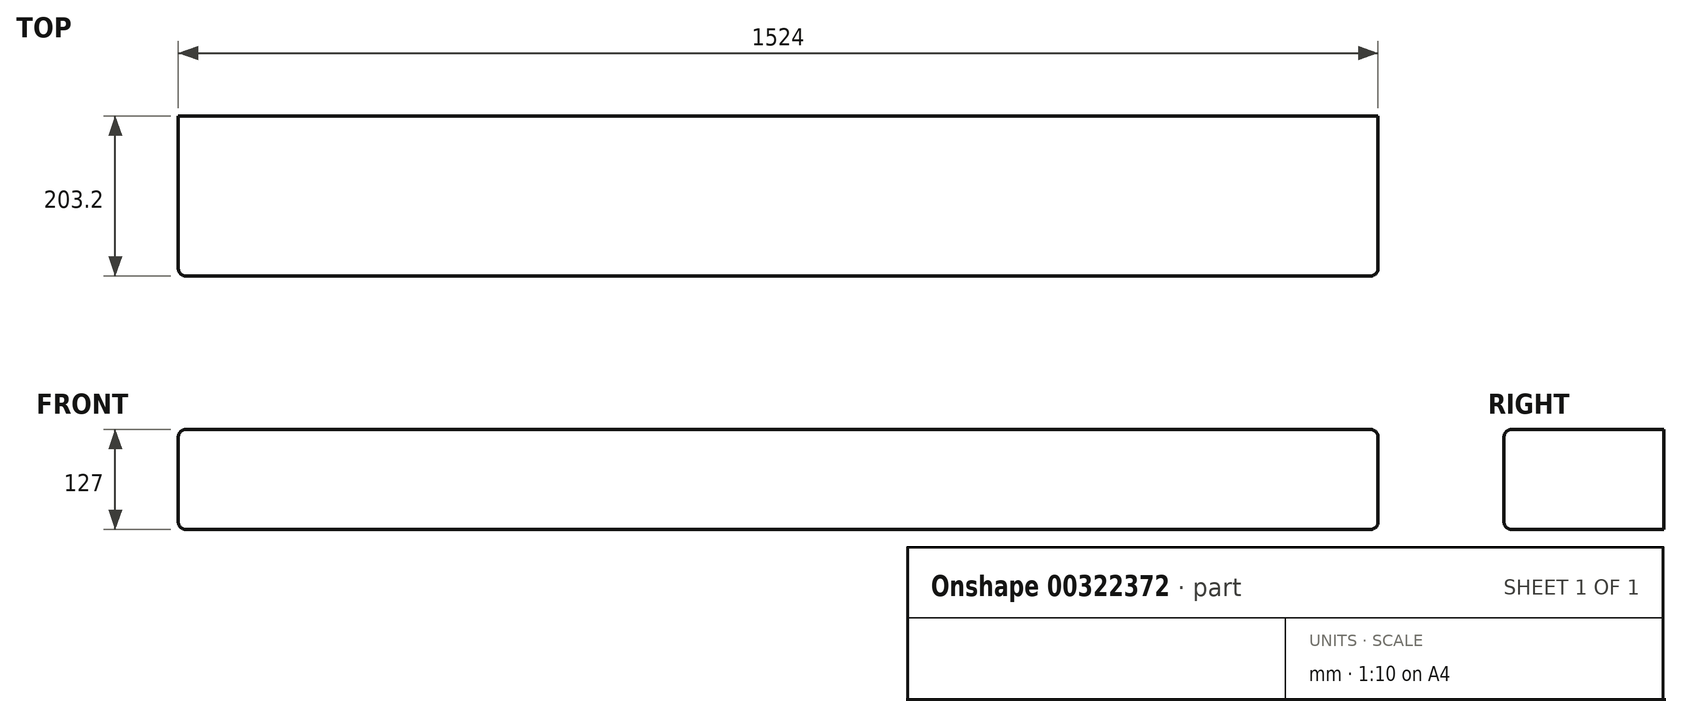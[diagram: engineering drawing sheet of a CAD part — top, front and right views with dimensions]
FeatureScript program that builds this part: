
annotation { "Feature Type Name" : "Feature", "Feature Type Description" : "" }
export const myFeature = defineFeature(function(context is Context, id is Id, definition is map)
    precondition{}
    {
        {
            var Q0;
            Q0=qCreatedBy(makeId("Right.planeOp"),FACE);
            var sketch = newSketch(context, id + "F0", { "sketchPlane" : qUnion([Q0])});
            skLineSegment(sketch, "E0.bottom", {"start": v(0, 0) * mm, "end": v(-203.2, 0) * mm});
            skLineSegment(sketch, "E0.top", {"start": v(0, 127) * mm, "end": v(-203.2, 127) * mm});
            skLineSegment(sketch, "E0.left", {"start": v(0, 0) * mm, "end": v(0, 127) * mm});
            skLineSegment(sketch, "E0.right", {"start": v(-203.2, 0) * mm, "end": v(-203.2, 127) * mm});
            skSolve(sketch);
        }
        {
            var Q0;
            Q0=makeQuery(id+"F0.imprint","IMPRINT",FACE,{"disambiguationData":[TD([[makeQuery(id+"F0.imprint","IMPRINT",EDGE,{"derivedFrom":sQuery(id+"F0.wireOp",EDGE,"E0.bottom")}),-1.0]])]});
            extrude(context, id + "F1", {"entities" : qUnion([Q0]), "endBound" : BoundingType.SYMMETRIC, "depth" : 1524 * mm});
        }
        {
            var Q0;
            Q0=makeQuery(id+"F1.opExtrude","SWEPT_EDGE",EDGE,{"disambiguationData":[OSD([sQuery(id+"F0.wireOp",EDGE,"E0.top"),sQuery(id+"F0.wireOp",EDGE,"E0.right")])]});
            var Q1;
            Q1=makeQuery(id+"F1.opExtrude","CAP_EDGE",EDGE,{"disambiguationData":[OSD([sQuery(id+"F0.wireOp",EDGE,"E0.top")])],"isStart":false});
            var Q2;
            Q2=makeQuery(id+"F1.opExtrude","CAP_EDGE",EDGE,{"disambiguationData":[OSD([sQuery(id+"F0.wireOp",EDGE,"E0.right")])],"isStart":false});
            var Q3;
            Q3=makeQuery(id+"F1.opExtrude","CAP_EDGE",EDGE,{"disambiguationData":[OSD([sQuery(id+"F0.wireOp",EDGE,"E0.bottom")])],"isStart":false});
            var Q4;
            Q4=makeQuery(id+"F1.opExtrude","SWEPT_EDGE",EDGE,{"disambiguationData":[OSD([sQuery(id+"F0.wireOp",EDGE,"E0.bottom"),sQuery(id+"F0.wireOp",EDGE,"E0.right")])]});
            var Q5;
            Q5=makeQuery(id+"F1.opExtrude","CAP_EDGE",EDGE,{"disambiguationData":[OSD([sQuery(id+"F0.wireOp",EDGE,"E0.right")])],"isStart":true});
            var Q6;
            Q6=makeQuery(id+"F1.opExtrude","CAP_EDGE",EDGE,{"disambiguationData":[OSD([sQuery(id+"F0.wireOp",EDGE,"E0.top")])],"isStart":true});
            var Q7;
            Q7=makeQuery(id+"F1.opExtrude","CAP_EDGE",EDGE,{"disambiguationData":[OSD([sQuery(id+"F0.wireOp",EDGE,"E0.bottom")])],"isStart":true});
            fillet(context, id + "F2", {"entities" : qUnion([Q0, Q1, Q2, Q3, Q4, Q5, Q6, Q7]), "radius" : 9.52 * mm, "tangentPropagation" : true, "allowEdgeOverflow" : false});
        }
    });
